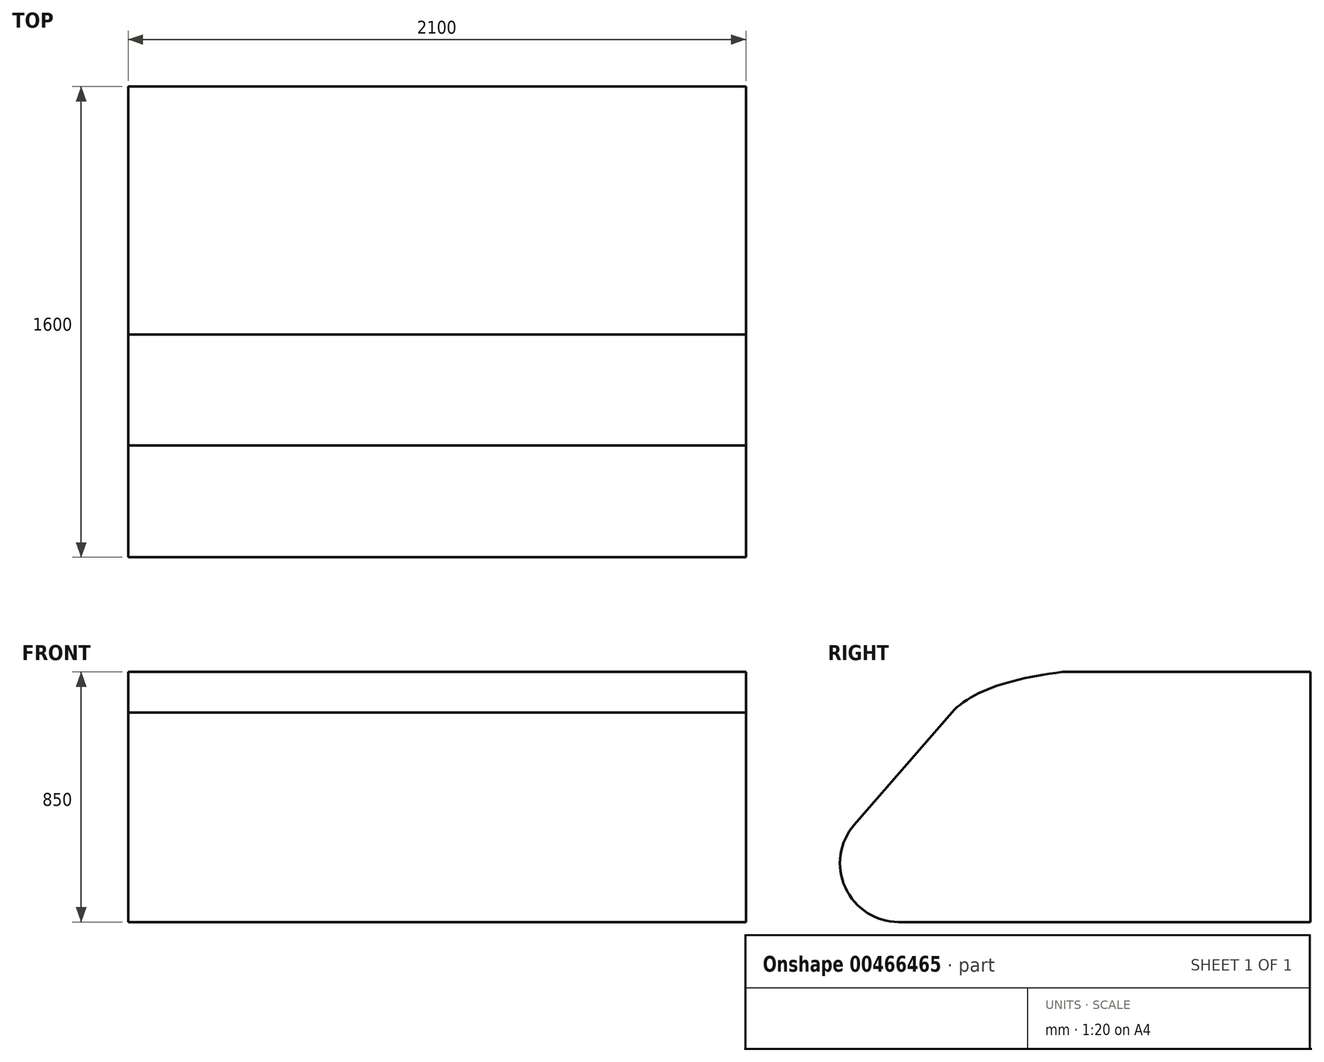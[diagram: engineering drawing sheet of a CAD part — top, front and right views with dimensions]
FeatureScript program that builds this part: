
annotation { "Feature Type Name" : "Feature", "Feature Type Description" : "" }
export const myFeature = defineFeature(function(context is Context, id is Id, definition is map)
    precondition{}
    {
        {
            var Q0;
            Q0=qCreatedBy(makeId("Right.planeOp"),FACE);
            var sketch = newSketch(context, id + "F0", { "sketchPlane" : qUnion([Q0])});
            skLineSegment(sketch, "E0", {"start": v(0, 0) * mm, "end": v(0, 850) * mm});
            skLineSegment(sketch, "E1", {"start": v(0, 0) * mm, "end": v(-1400, 0) * mm});
            skLineSegment(sketch, "E2", {"start": v(0, 850) * mm, "end": v(-917.7, 850) * mm});
            skLineSegment(sketch, "E3", {"start": v(-1516.7, 0) * mm, "end": v(-1516.7, 0) * mm});
            skLineSegment(sketch, "E4", {"start": v(-1550.95, 331.2) * mm, "end": v(-1219.6, 712.41) * mm});
            skPoint(sketch, "E5.orphan", {"position": v(-1400, 0) * mm});
            skPoint(sketch, "E6.visualSharp", {"position": v(-1838.84, 0) * mm});
            skArc(sketch, "E6.filletArc", {"start": v(-1550.95, 331.2) * mm, "mid": v(-1582, 117.06) * mm, "end": v(-1400, 0) * mm});
            skPoint(sketch, "E7.visualSharp", {"position": v(-1100, 850) * mm});
            skArc(sketch, "E7.filletArc", {"start": v(-917.7, 850) * mm, "mid": v(-1083.58, 813.98) * mm, "end": v(-1219.6, 712.41) * mm});
            skLineSegment(sketch, "E8", {"start": v(0, 750) * mm, "end": v(1000, 750) * mm});
            skFitSpline(sketch, "E9", {"points": [v(1000, 750) * mm, v(-1219.6, 712.41) * mm], "startDerivative": vector(-2482.92, 297.81) * mm, "endDerivative": vector(-702.82, -791.02) * mm});
            skSolve(sketch);
        }
        {
            var Q0;
            Q0=makeQuery(id+"F0.imprint","IMPRINT",FACE,{"disambiguationData":[TD([[makeQuery(id+"F0.imprint","IMPRINT",EDGE,{"derivedFrom":sQuery(id+"F0.wireOp",EDGE,"E0")}),1.0]])]});
            extrude(context, id + "F1", {"entities" : qUnion([Q0]), "depth" : 2100 * mm, "offsetDistance" : 25 * mm});
        }
    });
